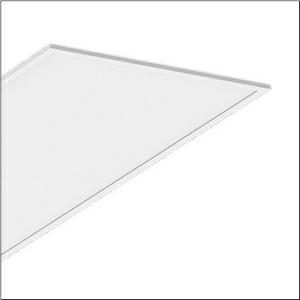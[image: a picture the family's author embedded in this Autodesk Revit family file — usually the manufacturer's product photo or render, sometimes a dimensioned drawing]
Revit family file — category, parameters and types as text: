
# Revit family: apollon_21_linear_51mq19wd2m14
name_source: partatom
category: Lighting Fixtures
units: mm (PartAtom-declared; Revit-internal decimal feet)

## family parameters
Cut with Voids When Loaded = No
Host = Face
Light Source = No
Part Type = Normal
Room Calculation Point = No
Round Connector Dimension = Use Diameter
Shared = No

## types (1)
- --- (1 x LED, 7000 lm, 44.6 W, 4000K)
    Apparent Load = 45 VA
    CIE Flux Codes = 60 87 97 100 100
    Color Rendering = 80
    Color Temperature = 4000K
    Default Elevation = 1800 mm
    Description = Apollon 21 linear, office luminaire, primary optical cover: micro prismatic cover, of PMMA, CAT 2 (L<= 3000cd/m²), light emission: direct distribution, primary light characteristic: symmetric, installation type: lay-in mounting, LED, rated luminous flux: 7.820lm, luminous efficacy: 173lm/W, light colour: 830/840, colour temperature: 3000/4000K, control gear: DALI 2, Multilumen, with terminal, 5-pole, mains connection: 220..240V, AC/DC, 0/50..60Hz, rated input power: 45.3W, suitable for self-contained emergency lighting element 59MQE002602A with integrated self-test function according to EN 60598-2-22, housing, of aluminium, coated, traffic white (RAL 9016), length: 1.245mm, width: 622mm, height: 55mm, recess depth: 180mm, housing upper side, of sheet steel, galvanised, protection rating (complete): IP20, protection rating (lamp compartment, on room side): IP50, insulation class (complete): insulation class II (safety insulation), certification: CE, ENEC, impact resistance: IK03, permissible operating ambient temperature: -20..+45°C, permissible storage temperature: -40..+80°C, standard: EN 60598-2-22, packaging unit: 1 piece
    Height = 0 mm  [stored 0 ft]
    Lamp = 1 x LED
    Lamp Light Flux = 7000 lm
    Lamp Power = 44.6 W
    Lamp count = 1
    Length = 1245 mm
    Luminous efficacy = 157 lm/W
    Manufacturer = Siteco
    ModVariant = No
    Model = 51MQ19WD2M14
    Mounting Place = Ceiling
    Mounting Type = Recessed
    Number of Poles = 1
    OnlyDefault = Yes
    Power Factor = 1
    Product Name = Apollon 21 linear
    Product group = office luminaire | ceiling recessed
    ProductGroupID = 400
    Protection Class = Protection class II
    Protection Degree = IP 20
    RLX_Detail_Level = 1
    RLX_Emergency_Light_Flux = 0 lm
    RLX_Emergency_Type = 0
    RLX_Emergency_Type_DB = No
    RlxData = <blob elided: 19721 chars, md5=6d24ee31>
    Socket = socket
    Standby Power = 0 W
    System Light Flux = 7000 lm
    System Power = 45 W
    Type Comments = factory setting
    Type Image = l_1335551.jpg
    URL = http://relux.com
    VarID = @adj_089561
    Voltage = 0 V
    Weight = 0.00 kg
    Width = 622 mm

note: [stored X ft] marks values corroborated as IEEE doubles in the binary element streams (Revit-internal decimal feet)

## geometry (parser evidence)
native form markers: Blend x4, Sweep x11
no freeform markers — native parametric forms only
